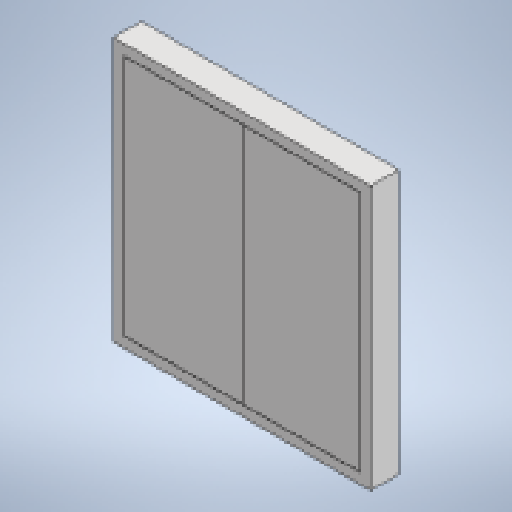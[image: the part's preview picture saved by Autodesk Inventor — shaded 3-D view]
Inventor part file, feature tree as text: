
AUTODESK INVENTOR PART (.ipt)
format: ipt  version: 2025 (Build 290162010, 162A)  size: 212,992 bytes
history: native  units: mm
features: extrude x7, sketch x7, projected_geometry x6
ambient origin geometry x8: Origin, YZ Plane, XZ Plane, XY Plane, X Axis, Y Axis, Z Axis, Center Point
bodies: Solid1 (feature_tree)
feature tree (20):
  extrude  "Extrusion1"  Depth=9100.0mm
  extrude  "Extrusion3"  Depth=650.0mm TaperAngle=0.0deg
  extrude  "Extrusion4"  Depth=10.0mm TaperAngle=0.0deg
  extrude  "Extrusion5"  Depth=10.0mm TaperAngle=0.0deg
  extrude  "Extrusion6"  Depth=1300.0mm
  extrude  "Extrusion7"  Depth=10.0mm TaperAngle=0.0deg
  extrude  "Extrusion10"  Depth=10.0mm
  sketch  "Sketch1"  dims[d0=8850.0mm d1=9100.0mm]
  sketch  "Sketch4"  dims[d3=400.0mm d4=650.0mm d5=0.0mm]
  projected_geometry  "Projected Loop2"
  sketch  "Sketch5"  dims[d10=400.0mm d11=0.0mm d19=10.0mm d20=0.0mm]
  projected_geometry  "Projected Loop3"
  sketch  "Sketch6"  dims[d21=4420.0mm d22=10.0mm d23=0.0mm]
  projected_geometry  "Projected Loop4"
  sketch  "Sketch7"  dims[d24=1100.0mm d25=1300.0mm]
  projected_geometry  "Projected Loop5"
  projected_geometry  "Projected Loop6"
  sketch  "Sketch8"  dims[d26=10.0mm d27=0.0mm d30=10.0mm d31=0.0mm]
  sketch  "Sketch12"  dims[d32=50.0mm d33=2050.0mm d34=850.0mm d35=2370.0mm d36=10.0mm d37=0.0mm d42=1.853479mm d43=1500.0mm d48=800.0mm d49=200.0mm d50=2.186689mm d51=1350.0mm d52=1500.0mm d53=0.0mm d54=1500.0mm d55=900.0mm]
  projected_geometry  "Projected Loop9"
